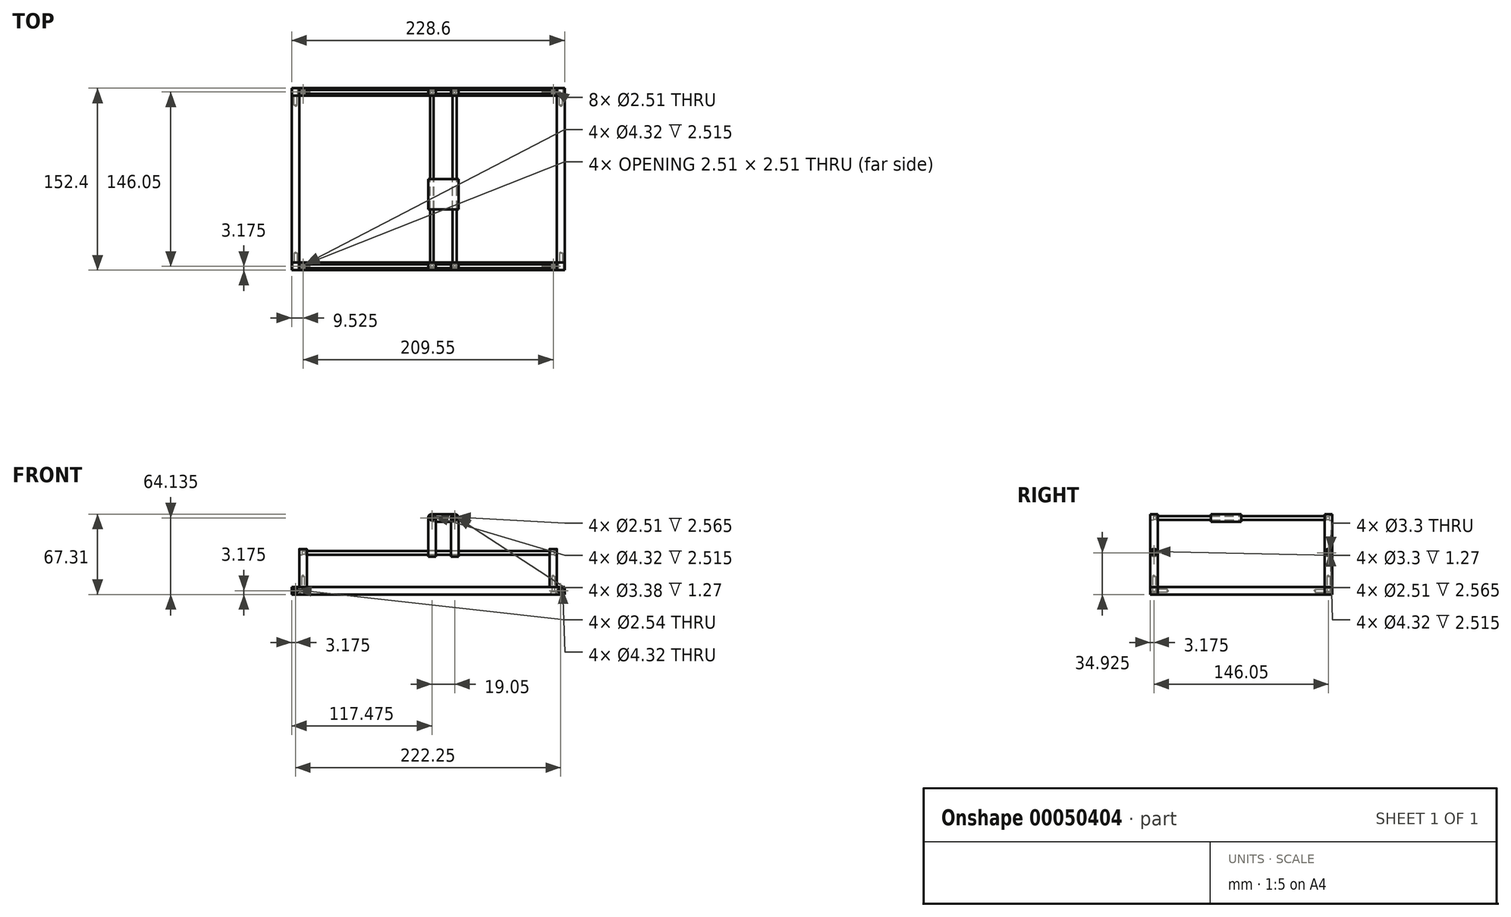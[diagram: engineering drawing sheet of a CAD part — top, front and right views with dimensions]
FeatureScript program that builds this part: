
annotation { "Feature Type Name" : "Feature", "Feature Type Description" : "" }
export const myFeature = defineFeature(function(context is Context, id is Id, definition is map)
    precondition{}
    {
        {
            var Q0;
            Q0=qCreatedBy(makeId("Top.planeOp"),FACE);
            var sketch = newSketch(context, id + "F0", { "sketchPlane" : qUnion([Q0])});
            skLineSegment(sketch, "E0.rect.bottom", {"start": v(107.95, -69.85) * mm, "end": v(-107.95, -69.85) * mm});
            skLineSegment(sketch, "E0.rect.top", {"start": v(107.95, 69.85) * mm, "end": v(-107.95, 69.85) * mm});
            skLineSegment(sketch, "E0.rect.left", {"start": v(107.95, -69.85) * mm, "end": v(107.95, 69.85) * mm});
            skLineSegment(sketch, "E0.rect.right", {"start": v(-107.95, -69.85) * mm, "end": v(-107.95, 69.85) * mm});
            skPoint(sketch, "E0.rect.middle", {"position": v(0, 0) * mm});
            skLineSegment(sketch, "E1.rect.bottom", {"start": v(114.3, -76.2) * mm, "end": v(-114.3, -76.2) * mm});
            skLineSegment(sketch, "E1.rect.top", {"start": v(114.3, 76.2) * mm, "end": v(-114.3, 76.2) * mm});
            skLineSegment(sketch, "E1.rect.left", {"start": v(114.3, -76.2) * mm, "end": v(114.3, 76.2) * mm});
            skLineSegment(sketch, "E1.rect.right", {"start": v(-114.3, -76.2) * mm, "end": v(-114.3, 76.2) * mm});
            skLineSegment(sketch, "E2", {"start": v(-107.95, 69.85) * mm, "end": v(-114.3, 69.85) * mm});
            skLineSegment(sketch, "E3", {"start": v(107.95, 69.85) * mm, "end": v(114.3, 69.85) * mm});
            skLineSegment(sketch, "E4", {"start": v(107.95, -69.85) * mm, "end": v(114.3, -69.85) * mm});
            skLineSegment(sketch, "E5", {"start": v(-107.95, -69.85) * mm, "end": v(-114.3, -69.85) * mm});
            skLineSegment(sketch, "E6", {"start": v(-107.95, 69.85) * mm, "end": v(-107.95, 76.2) * mm, "construction": true});
            skLineSegment(sketch, "E7", {"start": v(107.95, 69.85) * mm, "end": v(107.95, 76.2) * mm, "construction": true});
            skLineSegment(sketch, "E8", {"start": v(107.95, -69.85) * mm, "end": v(107.95, -76.2) * mm, "construction": true});
            skLineSegment(sketch, "E9", {"start": v(-107.95, -69.85) * mm, "end": v(-107.95, -76.2) * mm, "construction": true});
            skCircle(sketch, "E10", {"center": v(-104.78, 73.03) * mm, "radius": 2.16 * mm});
            skCircle(sketch, "E11.0.1.0", {"center": v(-104.78, -73.02) * mm, "radius": 2.16 * mm});
            skCircle(sketch, "E11.1.0.0", {"center": v(104.77, 73.03) * mm, "radius": 2.16 * mm});
            skCircle(sketch, "E11.1.1.0", {"center": v(104.77, -73.02) * mm, "radius": 2.16 * mm});
            skLineSegment(sketch, "E11.direction1", {"start": v(-104.78, 73.03) * mm, "end": v(104.77, 73.03) * mm, "construction": true});
            skLineSegment(sketch, "E11.direction2", {"start": v(-104.78, 73.03) * mm, "end": v(-104.78, -73.02) * mm, "construction": true});
            skSolve(sketch);
        }
        {
            var Q0;
            Q0=makeQuery(id+"F0.imprint","IMPRINT",FACE,{"disambiguationData":[TD([[makeQuery(id+"F0.imprint","IMPRINT",EDGE,{"derivedFrom":sQuery(id+"F0.wireOp",EDGE,"E0.rect.top")}),-1.0]])]});
            var Q1;
            Q1=makeQuery(id+"F0.imprint","IMPRINT",FACE,{"disambiguationData":[TD([[makeQuery(id+"F0.imprint","IMPRINT",EDGE,{"derivedFrom":sQuery(id+"F0.wireOp",EDGE,"E0.rect.bottom")}),1.0]])]});
            var Q2;
            Q2=makeQuery(id+"F0.imprint","IMPRINT",FACE,{"disambiguationData":[TD([[makeQuery(id+"F0.imprint","IMPRINT",EDGE,{"derivedFrom":sQuery(id+"F0.wireOp",EDGE,"E10")}),1.0]])]});
            var Q3;
            Q3=makeQuery(id+"F0.imprint","IMPRINT",FACE,{"disambiguationData":[TD([[makeQuery(id+"F0.imprint","IMPRINT",EDGE,{"derivedFrom":sQuery(id+"F0.wireOp",EDGE,"E11.1.0.0")}),1.0]])]});
            var Q4;
            Q4=makeQuery(id+"F0.imprint","IMPRINT",FACE,{"disambiguationData":[TD([[makeQuery(id+"F0.imprint","IMPRINT",EDGE,{"derivedFrom":sQuery(id+"F0.wireOp",EDGE,"E11.1.1.0")}),1.0]])]});
            var Q5;
            Q5=makeQuery(id+"F0.imprint","IMPRINT",FACE,{"disambiguationData":[TD([[makeQuery(id+"F0.imprint","IMPRINT",EDGE,{"derivedFrom":sQuery(id+"F0.wireOp",EDGE,"E11.0.1.0")}),1.0]])]});
            extrude(context, id + "F1", {"entities" : qUnion([Q0, Q1, Q2, Q3, Q4, Q5]), "depth" : 6.35 * mm});
        }
        {
            var Q0;
            Q0=makeQuery(id+"F0.imprint","IMPRINT",FACE,{"disambiguationData":[TD([[makeQuery(id+"F0.imprint","IMPRINT",EDGE,{"derivedFrom":sQuery(id+"F0.wireOp",EDGE,"E0.rect.right")}),1.0]])]});
            var Q1;
            Q1=makeQuery(id+"F0.imprint","IMPRINT",FACE,{"disambiguationData":[TD([[makeQuery(id+"F0.imprint","IMPRINT",EDGE,{"derivedFrom":sQuery(id+"F0.wireOp",EDGE,"E0.rect.left")}),-1.0]])]});
            extrude(context, id + "F2", {"entities" : qUnion([Q0, Q1]), "depth" : 6.35 * mm});
        }
        {
            var Q0;
            Q0=makeQuery(id+"F1.opExtrude","SWEPT_FACE",FACE,{"disambiguationData":[OSD([sQuery(id+"F0.wireOp",EDGE,"E1.rect.top")])]});
            var sketch = newSketch(context, id + "F3", { "sketchPlane" : qUnion([Q0])});
            skCircle(sketch, "E12", {"center": v(-111.13, 3.18) * mm, "radius": 2.38 * mm});
            skLineSegment(sketch, "E13", {"start": v(0, 20.14) * mm, "end": v(0, -20.13) * mm, "construction": true});
            skCircle(sketch, "E14", {"center": v(-111.13, 3.18) * mm, "radius": 1.59 * mm});
            skCircle(sketch, "E15.MirrorC", {"center": v(111.13, 3.18) * mm, "radius": 1.59 * mm});
            skCircle(sketch, "E16.MirrorC", {"center": v(111.13, 3.18) * mm, "radius": 2.38 * mm});
            skSolve(sketch);
        }
        {
            var Q0;
            Q0=makeQuery(id+"F1.opExtrude","SWEPT_FACE",FACE,{"disambiguationData":[OSD([sQuery(id+"F0.wireOp",EDGE,"E1.rect.bottom")])]});
            var sketch = newSketch(context, id + "F4", { "sketchPlane" : qUnion([Q0])});
            skCircle(sketch, "E17.0", {"center": v(-111.13, 3.18) * mm, "radius": 2.38 * mm});
            skCircle(sketch, "E18.0", {"center": v(-111.13, 3.18) * mm, "radius": 1.59 * mm});
            skCircle(sketch, "E19.0", {"center": v(111.13, 3.18) * mm, "radius": 2.38 * mm});
            skCircle(sketch, "E20.0", {"center": v(111.13, 3.18) * mm, "radius": 1.59 * mm});
            skSolve(sketch);
        }
        {
            var Q0;
            Q0=sQuery(id+"F4.wireOp",VERTEX,"E19.0.center");
            var Q1;
            Q1=sQuery(id+"F4.wireOp",VERTEX,"E17.0.center");
            var Q2;
            Q2=sQuery(id+"F3.wireOp",VERTEX,"E15.MirrorC.center");
            var Q3;
            Q3=sQuery(id+"F3.wireOp",VERTEX,"E12.center");
            var Q4;
            Q4=makeQuery(id+"F1.opExtrude","SWEPT_BODY",BODY,{"disambiguationData":[OSD([sQuery(id+"F0.wireOp",EDGE,"E0.rect.bottom"),sQuery(id+"F0.wireOp",EDGE,"E1.rect.bottom"),sQuery(id+"F0.wireOp",EDGE,"E1.rect.left"),sQuery(id+"F0.wireOp",EDGE,"E1.rect.right"),sQuery(id+"F0.wireOp",EDGE,"E4"),sQuery(id+"F0.wireOp",EDGE,"E5")])]});
            var Q5;
            Q5=makeQuery(id+"F1.opExtrude","SWEPT_BODY",BODY,{"disambiguationData":[OSD([sQuery(id+"F0.wireOp",EDGE,"E0.rect.top"),sQuery(id+"F0.wireOp",EDGE,"E1.rect.top"),sQuery(id+"F0.wireOp",EDGE,"E1.rect.left"),sQuery(id+"F0.wireOp",EDGE,"E1.rect.right"),sQuery(id+"F0.wireOp",EDGE,"E2"),sQuery(id+"F0.wireOp",EDGE,"E3")])]});
            var Q6;
            Q6=makeQuery(id+"F2.opExtrude","SWEPT_BODY",BODY,{"disambiguationData":[OSD([sQuery(id+"F0.wireOp",EDGE,"E0.rect.left"),sQuery(id+"F0.wireOp",EDGE,"E1.rect.left"),sQuery(id+"F0.wireOp",EDGE,"E3"),sQuery(id+"F0.wireOp",EDGE,"E4")])]});
            var Q7;
            Q7=makeQuery(id+"F2.opExtrude","SWEPT_BODY",BODY,{"disambiguationData":[OSD([sQuery(id+"F0.wireOp",EDGE,"E0.rect.right"),sQuery(id+"F0.wireOp",EDGE,"E1.rect.right"),sQuery(id+"F0.wireOp",EDGE,"E2"),sQuery(id+"F0.wireOp",EDGE,"E5")])]});
            hole(context, id + "F5", {"style" : HoleStyle.C_BORE, "holeDiameter" : 2.54 * mm, "cBoreDiameter" : 4.32 * mm, "cBoreDepth" : 6.35 * mm, "endStyle" : HoleEndStyle.BLIND, "holeDepth" : 14.29 * mm, "locations" : qUnion([Q0, Q1, Q2, Q3]), "scope" : qUnion([Q4, Q5, Q6, Q7])});
        }
        {
            var Q0;
            Q0=makeQuery(id+"F1.opExtrude","CAP_FACE",FACE,{"disambiguationData":[OSD([sQuery(id+"F0.wireOp",EDGE,"E0.rect.top"),sQuery(id+"F0.wireOp",EDGE,"E1.rect.top"),sQuery(id+"F0.wireOp",EDGE,"E1.rect.left"),sQuery(id+"F0.wireOp",EDGE,"E1.rect.right"),sQuery(id+"F0.wireOp",EDGE,"E2"),sQuery(id+"F0.wireOp",EDGE,"E3")])],"isStart":false});
            var sketch = newSketch(context, id + "F6", { "sketchPlane" : qUnion([Q0])});
            skLineSegment(sketch, "E21.rect.bottom", {"start": v(-101.6, 69.85) * mm, "end": v(-107.95, 69.85) * mm});
            skLineSegment(sketch, "E21.rect.top", {"start": v(-101.6, 76.2) * mm, "end": v(-107.95, 76.2) * mm});
            skLineSegment(sketch, "E21.rect.left", {"start": v(-101.6, 69.85) * mm, "end": v(-101.6, 76.2) * mm});
            skLineSegment(sketch, "E21.rect.right", {"start": v(-107.95, 69.85) * mm, "end": v(-107.95, 76.2) * mm});
            skPoint(sketch, "E21.rect.middle", {"position": v(-104.78, 73.02) * mm});
            skSolve(sketch);
        }
        {
            var Q0;
            Q0 = qSketchRegion(id + "F6", true);
            extrude(context, id + "F7", {"entities" : qUnion([Q0]), "depth" : 31.75 * mm});
        }
        {
            var Q0;
            Q0=makeQuery(id+"F7.opExtrude","CAP_EDGE",EDGE,{"disambiguationData":[OSD([sQuery(id+"F6.wireOp",EDGE,"E21.rect.bottom")])],"isStart":false});
            var Q1;
            Q1=makeQuery(id+"F7.opExtrude","CAP_EDGE",EDGE,{"disambiguationData":[OSD([sQuery(id+"F6.wireOp",EDGE,"E21.rect.top")])],"isStart":false});
            fillet(context, id + "F8", {"entities" : qUnion([Q0, Q1]), "radius" : 3.17 * mm, "tangentPropagation" : true, "allowEdgeOverflow" : false});
        }
        {
            var Q0;
            Q0=sQuery(id+"F0.wireOp",VERTEX,"E11.0.1.0.center");
            var Q1;
            Q1=sQuery(id+"F0.wireOp",VERTEX,"E11.1.1.0.center");
            var Q2;
            Q2=sQuery(id+"F0.wireOp",VERTEX,"E11.1.0.0.center");
            var Q3;
            Q3=sQuery(id+"F0.wireOp",VERTEX,"E11.direction1.start");
            var Q4;
            Q4=makeQuery(id+"F1.opExtrude","SWEPT_BODY",BODY,{"disambiguationData":[OSD([sQuery(id+"F0.wireOp",EDGE,"E0.rect.bottom"),sQuery(id+"F0.wireOp",EDGE,"E1.rect.bottom"),sQuery(id+"F0.wireOp",EDGE,"E1.rect.left"),sQuery(id+"F0.wireOp",EDGE,"E1.rect.right"),sQuery(id+"F0.wireOp",EDGE,"E4"),sQuery(id+"F0.wireOp",EDGE,"E5")])]});
            var Q5;
            Q5=makeQuery(id+"F1.opExtrude","SWEPT_BODY",BODY,{"disambiguationData":[OSD([sQuery(id+"F0.wireOp",EDGE,"E0.rect.top"),sQuery(id+"F0.wireOp",EDGE,"E1.rect.top"),sQuery(id+"F0.wireOp",EDGE,"E1.rect.left"),sQuery(id+"F0.wireOp",EDGE,"E1.rect.right"),sQuery(id+"F0.wireOp",EDGE,"E2"),sQuery(id+"F0.wireOp",EDGE,"E3")])]});
            var Q6;
            Q6=makeQuery(id+"FoTdJiMAjfuwymy_5.opPattern","COPY",BODY,{"derivedFrom":makeQuery(id+"F7.opExtrude","SWEPT_BODY",BODY,{"disambiguationData":[OSD([sQuery(id+"F6.wireOp",EDGE,"E21.rect.bottom"),sQuery(id+"F6.wireOp",EDGE,"E21.rect.top"),sQuery(id+"F6.wireOp",EDGE,"E21.rect.left"),sQuery(id+"F6.wireOp",EDGE,"E21.rect.right")])]}),"instanceName":"0_1"});
            var Q7;
            Q7=makeQuery(id+"FoTdJiMAjfuwymy_5.opPattern","COPY",BODY,{"derivedFrom":makeQuery(id+"F7.opExtrude","SWEPT_BODY",BODY,{"disambiguationData":[OSD([sQuery(id+"F6.wireOp",EDGE,"E21.rect.bottom"),sQuery(id+"F6.wireOp",EDGE,"E21.rect.top"),sQuery(id+"F6.wireOp",EDGE,"E21.rect.left"),sQuery(id+"F6.wireOp",EDGE,"E21.rect.right")])]}),"instanceName":"1_1"});
            var Q8;
            Q8=makeQuery(id+"F7.opExtrude","SWEPT_BODY",BODY,{"disambiguationData":[OSD([sQuery(id+"F6.wireOp",EDGE,"E21.rect.bottom"),sQuery(id+"F6.wireOp",EDGE,"E21.rect.top"),sQuery(id+"F6.wireOp",EDGE,"E21.rect.left"),sQuery(id+"F6.wireOp",EDGE,"E21.rect.right")])]});
            var Q9;
            Q9=makeQuery(id+"FoTdJiMAjfuwymy_5.opPattern","COPY",BODY,{"derivedFrom":makeQuery(id+"F7.opExtrude","SWEPT_BODY",BODY,{"disambiguationData":[OSD([sQuery(id+"F6.wireOp",EDGE,"E21.rect.bottom"),sQuery(id+"F6.wireOp",EDGE,"E21.rect.top"),sQuery(id+"F6.wireOp",EDGE,"E21.rect.left"),sQuery(id+"F6.wireOp",EDGE,"E21.rect.right")])]}),"instanceName":"1"});
            hole(context, id + "F9", {"style" : HoleStyle.C_BORE, "holeDiameter" : 2.5 * mm, "cBoreDiameter" : 4.32 * mm, "cBoreDepth" : 2.5 * mm, "endStyle" : HoleEndStyle.BLIND, "oppositeDirection" : true, "holeDepth" : 15.21 * mm, "locations" : qUnion([Q0, Q1, Q2, Q3]), "scope" : qUnion([Q4, Q5, Q6, Q7, Q8, Q9])});
        }
        {
            var Q0;
            Q0=makeQuery(id+"F7.opExtrude","SWEPT_FACE",FACE,{"disambiguationData":[OSD([sQuery(id+"F6.wireOp",EDGE,"E21.rect.left")])]});
            var sketch = newSketch(context, id + "F10", { "sketchPlane" : qUnion([Q0])});
            skCircle(sketch, "E22", {"center": v(73.02, 34.93) * mm, "radius": 1.65 * mm});
            skSolve(sketch);
        }
        {
            var Q0;
            Q0=makeQuery(id+"F10.imprint","IMPRINT",FACE,{"disambiguationData":[TD([[makeQuery(id+"F10.imprint","IMPRINT",EDGE,{"derivedFrom":sQuery(id+"F10.wireOp",EDGE,"E22")}),1.0]])]});
            extrude(context, id + "F11", {"entities" : qUnion([Q0]), "operationType" : NewBodyOperationType.REMOVE, "oppositeDirection" : true, "depth" : 1.27 * mm});
        }
        {
            var Q0;
            Q0=makeQuery(id+"F7.opExtrude","SWEPT_FACE",FACE,{"disambiguationData":[OSD([sQuery(id+"F6.wireOp",EDGE,"E21.rect.right")])]});
            var sketch = newSketch(context, id + "F12", { "sketchPlane" : qUnion([Q0])});
            skCircle(sketch, "E23.0", {"center": v(-73.02, 34.93) * mm, "radius": 1.65 * mm});
            skSolve(sketch);
        }
        {
            var Q0;
            Q0=sQuery(id+"F12.wireOp",VERTEX,"E23.0.center");
            var Q1;
            Q1=makeQuery(id+"F7.opExtrude","SWEPT_BODY",BODY,{"disambiguationData":[OSD([sQuery(id+"F6.wireOp",EDGE,"E21.rect.bottom"),sQuery(id+"F6.wireOp",EDGE,"E21.rect.top"),sQuery(id+"F6.wireOp",EDGE,"E21.rect.left"),sQuery(id+"F6.wireOp",EDGE,"E21.rect.right")])]});
            hole(context, id + "F13", {"style" : HoleStyle.C_BORE, "holeDiameter" : 2.5 * mm, "cBoreDiameter" : 4.32 * mm, "cBoreDepth" : 2.5 * mm, "endStyle" : HoleEndStyle.THROUGH, "locations" : qUnion([Q0]), "scope" : qUnion([Q1])});
        }
        {
            var Q0;
            Q0=qCreatedBy(makeId("Right.planeOp"),FACE);
            var sketch = newSketch(context, id + "F14", { "sketchPlane" : qUnion([Q0])});
            skCircle(sketch, "E24.0", {"center": v(73.03, 34.93) * mm, "radius": 2.16 * mm, "construction": true});
            skCircle(sketch, "E25", {"center": v(73.03, 34.93) * mm, "radius": 1.59 * mm});
            skSolve(sketch);
        }
        {
            var Q0;
            Q0=makeQuery(id+"F14.imprint","IMPRINT",FACE,{"disambiguationData":[TD([[makeQuery(id+"F14.imprint","IMPRINT",EDGE,{"derivedFrom":sQuery(id+"F14.wireOp",EDGE,"E25")}),1.0]])]});
            extrude(context, id + "F15", {"entities" : qUnion([Q0]), "endBound" : BoundingType.SYMMETRIC, "depth" : 205.74 * mm});
        }
        {
            var Q0;
            Q0=makeQuery(id+"F7.opExtrude","SWEPT_BODY",BODY,{"disambiguationData":[OSD([sQuery(id+"F6.wireOp",EDGE,"E21.rect.bottom"),sQuery(id+"F6.wireOp",EDGE,"E21.rect.top"),sQuery(id+"F6.wireOp",EDGE,"E21.rect.left"),sQuery(id+"F6.wireOp",EDGE,"E21.rect.right")])]});
            var Q1;
            Q1=qCreatedBy(makeId("Right.planeOp"),FACE);
            mirror(context, id + "F16", {"entities" : qUnion([Q0]), "mirrorPlane" : qUnion([Q1])});
        }
        {
            var Q0;
            Q0=makeQuery(id+"F16.opPattern","COPY",BODY,{"derivedFrom":makeQuery(id+"F7.opExtrude","SWEPT_BODY",BODY,{"disambiguationData":[OSD([sQuery(id+"F6.wireOp",EDGE,"E21.rect.bottom"),sQuery(id+"F6.wireOp",EDGE,"E21.rect.top"),sQuery(id+"F6.wireOp",EDGE,"E21.rect.left"),sQuery(id+"F6.wireOp",EDGE,"E21.rect.right")])]}),"instanceName":"1"});
            var Q1;
            Q1=makeQuery(id+"F7.opExtrude","SWEPT_BODY",BODY,{"disambiguationData":[OSD([sQuery(id+"F6.wireOp",EDGE,"E21.rect.bottom"),sQuery(id+"F6.wireOp",EDGE,"E21.rect.top"),sQuery(id+"F6.wireOp",EDGE,"E21.rect.left"),sQuery(id+"F6.wireOp",EDGE,"E21.rect.right")])]});
            var Q2;
            Q2=makeQuery(id+"F15.opExtrude","SWEPT_BODY",BODY,{"disambiguationData":[OSD([sQuery(id+"F14.wireOp",EDGE,"E25")])]});
            var Q3;
            Q3=qCreatedBy(makeId("Front.planeOp"),FACE);
            mirror(context, id + "F17", {"entities" : qUnion([Q0, Q1, Q2]), "mirrorPlane" : qUnion([Q3])});
        }
        {
            var Q0;
            Q0=qCreatedBy(makeId("Right.planeOp"),FACE);
            var sketch = newSketch(context, id + "F18", { "sketchPlane" : qUnion([Q0])});
            skCircle(sketch, "E26.0", {"center": v(73.02, 34.93) * mm, "radius": 1.65 * mm});
            skCircle(sketch, "E27", {"center": v(73.02, 34.93) * mm, "radius": 3.18 * mm});
            skLineSegment(sketch, "E28", {"start": v(73.02, 34.93) * mm, "end": v(73.02, 53.3) * mm});
            skLineSegment(sketch, "E29", {"start": v(69.85, 67.31) * mm, "end": v(76.2, 67.31) * mm});
            skLineSegment(sketch, "E30", {"start": v(76.2, 67.31) * mm, "end": v(76.2, 34.93) * mm});
            skLineSegment(sketch, "E31", {"start": v(69.85, 67.31) * mm, "end": v(69.85, 34.93) * mm});
            skSolve(sketch);
        }
        {
            var Q0;
            Q0 = qSketchRegion(id + "F18", true);
            extrude(context, id + "F19", {"entities" : qUnion([Q0]), "depth" : 6.35 * mm});
        }
        {
            var Q0;
            Q0=makeQuery(id+"F19.opExtrude","SWEPT_FACE",FACE,{"disambiguationData":[OSD([sQuery(id+"F18.wireOp",EDGE,"E30")])]});
            var sketch = newSketch(context, id + "F20", { "sketchPlane" : qUnion([Q0])});
            skPoint(sketch, "E32.centerSnap0", {"position": v(-3.18, 67.3) * mm});
            skCircle(sketch, "E33", {"center": v(-3.18, 64.13) * mm, "radius": 1.65 * mm, "construction": true});
            skArc(sketch, "E34", {"start": v(0, 64.13) * mm, "mid": v(-3.18, 67.31) * mm, "end": v(-6.35, 64.13) * mm});
            skLineSegment(sketch, "E35", {"start": v(0, 64.13) * mm, "end": v(0, 67.3) * mm});
            skLineSegment(sketch, "E36", {"start": v(0, 67.3) * mm, "end": v(-6.35, 67.3) * mm});
            skLineSegment(sketch, "E37", {"start": v(-6.35, 67.3) * mm, "end": v(-6.35, 64.13) * mm});
            skSolve(sketch);
        }
        {
            var Q0;
            {var subQ0=sQuery(id+"F20.wireOp",EDGE,"E37");Q0=makeQuery(id+"F20.imprint","IMPRINT",FACE,{"disambiguationData":[TD([[makeQuery(id+"F20.imprint","IMPRINT",EDGE,{"derivedFrom":subQ0}),1.0]])]});}
            var Q1;
            {var subQ0=sQuery(id+"F20.wireOp",EDGE,"E35");Q1=makeQuery(id+"F20.imprint","IMPRINT",FACE,{"disambiguationData":[TD([[makeQuery(id+"F20.imprint","IMPRINT",EDGE,{"derivedFrom":subQ0}),-1.0]])]});}
            var Q2;
            Q2=makeQuery(id+"F20.imprint","IMPRINT",FACE,{"disambiguationData":[TD([[makeQuery(id+"F20.imprint","IMPRINT",EDGE,{"derivedFrom":sQuery(id+"F20.wireOp",EDGE,"E33")}),1.0]])]});
            extrude(context, id + "F21", {"entities" : qUnion([Q0, Q1, Q2]), "operationType" : NewBodyOperationType.REMOVE, "endBound" : BoundingType.UP_TO_NEXT, "oppositeDirection" : true, "depth" : 25.4 * mm});
        }
        {
            var Q0;
            Q0=sQuery(id+"F20.wireOp",VERTEX,"E33.center");
            var Q1;
            Q1=makeQuery(id+"F19.opExtrude","SWEPT_BODY",BODY,{"disambiguationData":[OSD([sQuery(id+"F18.wireOp",EDGE,"E26.0"),sQuery(id+"F18.wireOp",EDGE,"E27"),sQuery(id+"F18.wireOp",EDGE,"E29"),sQuery(id+"F18.wireOp",EDGE,"E30"),sQuery(id+"F18.wireOp",EDGE,"E31")])]});
            hole(context, id + "F22", {"style" : HoleStyle.C_BORE, "holeDiameter" : 2.5 * mm, "cBoreDiameter" : 4.32 * mm, "cBoreDepth" : 2.5 * mm, "endStyle" : HoleEndStyle.THROUGH, "locations" : qUnion([Q0]), "scope" : qUnion([Q1])});
        }
        {
            var Q0;
            Q0=makeQuery(id+"F19.opExtrude","SWEPT_FACE",FACE,{"disambiguationData":[OSD([sQuery(id+"F18.wireOp",EDGE,"E31")])]});
            var sketch = newSketch(context, id + "F23", { "sketchPlane" : qUnion([Q0])});
            skCircle(sketch, "E38", {"center": v(3.18, 64.14) * mm, "radius": 1.69 * mm});
            skSolve(sketch);
        }
        {
            var Q0;
            Q0=makeQuery(id+"F23.imprint","IMPRINT",FACE,{"disambiguationData":[TD([[makeQuery(id+"F23.imprint","IMPRINT",EDGE,{"derivedFrom":sQuery(id+"F23.wireOp",EDGE,"E38")}),1.0]])]});
            extrude(context, id + "F24", {"entities" : qUnion([Q0]), "operationType" : NewBodyOperationType.REMOVE, "oppositeDirection" : true, "depth" : 1.27 * mm});
        }
        {
            var Q0;
            Q0=qCreatedBy(makeId("Right.planeOp"),FACE);
            cPlane(context, id + "F25", {"entities" : qUnion([Q0]), "cplaneType" : CPlaneType.OFFSET, "offset" : 12.7 * mm, "width" : 152.4 * mm, "height" : 152.4 * mm});
        }
        {
            var Q0;
            Q0=makeQuery(id+"F19.opExtrude","SWEPT_BODY",BODY,{"disambiguationData":[OSD([sQuery(id+"F18.wireOp",EDGE,"E26.0"),sQuery(id+"F18.wireOp",EDGE,"E27"),sQuery(id+"F18.wireOp",EDGE,"E29"),sQuery(id+"F18.wireOp",EDGE,"E30"),sQuery(id+"F18.wireOp",EDGE,"E31")])]});
            var Q1;
            Q1=qCreatedBy(id+"F25.planeOp",FACE);
            mirror(context, id + "F26", {"entities" : qUnion([Q0]), "mirrorPlane" : qUnion([Q1])});
        }
        {
            var Q0;
            Q0=makeQuery(id+"F26.opPattern","COPY",BODY,{"derivedFrom":makeQuery(id+"F19.opExtrude","SWEPT_BODY",BODY,{"disambiguationData":[OSD([sQuery(id+"F18.wireOp",EDGE,"E26.0"),sQuery(id+"F18.wireOp",EDGE,"E27"),sQuery(id+"F18.wireOp",EDGE,"E29"),sQuery(id+"F18.wireOp",EDGE,"E30"),sQuery(id+"F18.wireOp",EDGE,"E31")])]}),"instanceName":"1"});
            var Q1;
            Q1=makeQuery(id+"F19.opExtrude","SWEPT_BODY",BODY,{"disambiguationData":[OSD([sQuery(id+"F18.wireOp",EDGE,"E26.0"),sQuery(id+"F18.wireOp",EDGE,"E27"),sQuery(id+"F18.wireOp",EDGE,"E29"),sQuery(id+"F18.wireOp",EDGE,"E30"),sQuery(id+"F18.wireOp",EDGE,"E31")])]});
            var Q2;
            Q2=qCreatedBy(makeId("Front.planeOp"),FACE);
            mirror(context, id + "F27", {"entities" : qUnion([Q0, Q1]), "mirrorPlane" : qUnion([Q2])});
        }
        {
            var Q0;
            Q0=qCreatedBy(makeId("Front.planeOp"),FACE);
            var sketch = newSketch(context, id + "F28", { "sketchPlane" : qUnion([Q0])});
            skCircle(sketch, "E39.1", {"center": v(22.23, 64.14) * mm, "radius": 1.69 * mm, "construction": true});
            skCircle(sketch, "E39.2", {"center": v(3.18, 64.14) * mm, "radius": 1.69 * mm, "construction": true});
            skCircle(sketch, "E40", {"center": v(22.23, 64.14) * mm, "radius": 1.59 * mm});
            skCircle(sketch, "E41", {"center": v(3.18, 64.14) * mm, "radius": 1.59 * mm});
            skSolve(sketch);
        }
        {
            var Q0;
            Q0=makeQuery(id+"F28.imprint","IMPRINT",FACE,{"disambiguationData":[TD([[makeQuery(id+"F28.imprint","IMPRINT",EDGE,{"derivedFrom":sQuery(id+"F28.wireOp",EDGE,"E40")}),1.0]])]});
            var Q1;
            Q1=makeQuery(id+"F28.imprint","IMPRINT",FACE,{"disambiguationData":[TD([[makeQuery(id+"F28.imprint","IMPRINT",EDGE,{"derivedFrom":sQuery(id+"F28.wireOp",EDGE,"E41")}),1.0]])]});
            extrude(context, id + "F29", {"entities" : qUnion([Q0, Q1]), "endBound" : BoundingType.SYMMETRIC, "depth" : 142.24 * mm});
        }
        {
            var Q0;
            Q0=qCreatedBy(makeId("Front.planeOp"),FACE);
            var sketch = newSketch(context, id + "F30", { "sketchPlane" : qUnion([Q0])});
            skCircle(sketch, "E42.1", {"center": v(3.18, 64.14) * mm, "radius": 1.59 * mm, "construction": true});
            skCircle(sketch, "E43.0", {"center": v(22.23, 64.14) * mm, "radius": 1.59 * mm, "construction": true});
            skCircle(sketch, "E44", {"center": v(3.18, 64.14) * mm, "radius": 1.65 * mm});
            skCircle(sketch, "E45", {"center": v(22.23, 64.14) * mm, "radius": 1.65 * mm});
            skLineSegment(sketch, "E46", {"start": v(3.18, 64.14) * mm, "end": v(22.23, 64.14) * mm, "construction": true});
            skArc(sketch, "E47", {"start": v(3.17, 67.31) * mm, "mid": v(0, 64.14) * mm, "end": v(3.18, 60.96) * mm});
            skArc(sketch, "E48", {"start": v(22.23, 60.96) * mm, "mid": v(25.4, 64.14) * mm, "end": v(22.23, 67.31) * mm});
            skLineSegment(sketch, "E49", {"start": v(3.18, 67.31) * mm, "end": v(22.23, 67.31) * mm});
            skLineSegment(sketch, "E50", {"start": v(22.23, 60.96) * mm, "end": v(3.18, 60.96) * mm});
            skSolve(sketch);
        }
        {
            var Q0;
            Q0=makeQuery(id+"F30.imprint","IMPRINT",FACE,{"disambiguationData":[TD([[makeQuery(id+"F30.imprint","IMPRINT",EDGE,{"derivedFrom":sQuery(id+"F30.wireOp",EDGE,"E44")}),-1.0]])]});
            extrude(context, id + "F31", {"entities" : qUnion([Q0]), "depth" : 25.4 * mm});
        }
    });
